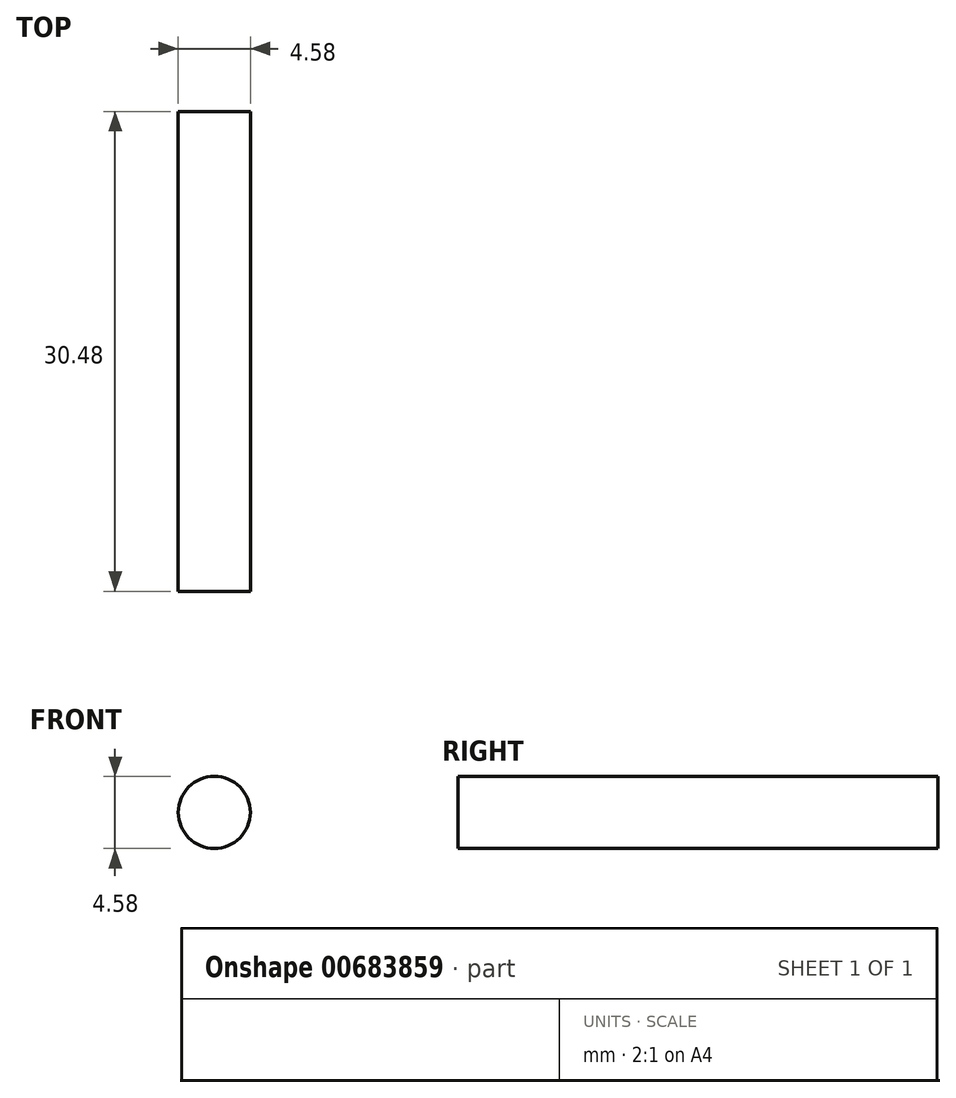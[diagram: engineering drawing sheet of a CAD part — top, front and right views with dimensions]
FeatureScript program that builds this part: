
annotation { "Feature Type Name" : "Feature", "Feature Type Description" : "" }
export const myFeature = defineFeature(function(context is Context, id is Id, definition is map)
    precondition{}
    {
        {
            var Q0;
            Q0=qCreatedBy(makeId("Front.planeOp"),FACE);
            var sketch = newSketch(context, id + "F0", { "sketchPlane" : qUnion([Q0])});
            skCircle(sketch, "E0", {"center": v(0, 0) * mm, "radius": 2.3 * mm});
            skSolve(sketch);
        }
        {
            var Q0;
            Q0=makeQuery(id+"F0.imprint","IMPRINT",FACE,{"disambiguationData":[TD([[makeQuery(id+"F0.imprint","IMPRINT",EDGE,{"derivedFrom":sQuery(id+"F0.wireOp",EDGE,"E0")}),1.0]])]});
            extrude(context, id + "F1", {"entities" : qUnion([Q0]), "depth" : 15.24 * mm, "offsetDistance" : 25.4 * mm, "hasSecondDirection" : true, "secondDirectionOppositeDirection" : true, "secondDirectionDepth" : 15.24 * mm});
        }
    });
